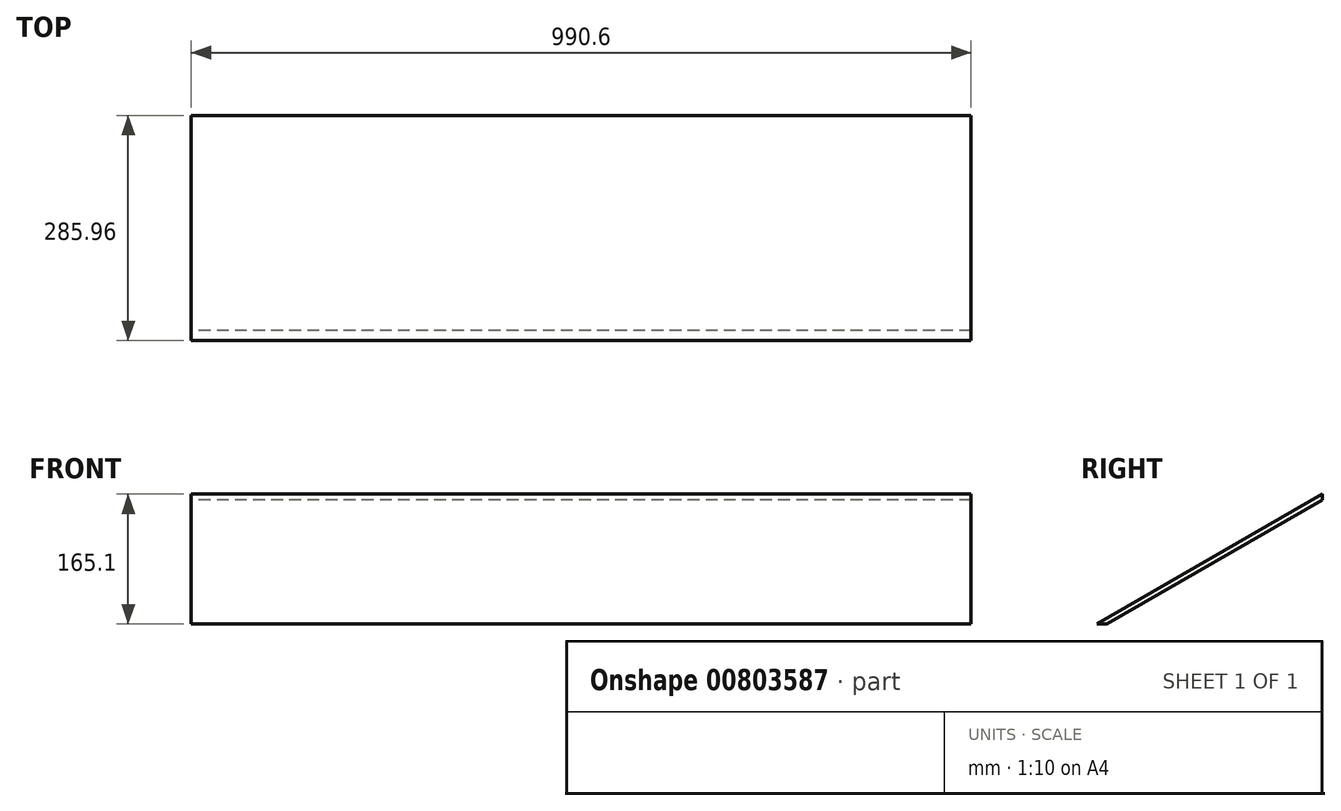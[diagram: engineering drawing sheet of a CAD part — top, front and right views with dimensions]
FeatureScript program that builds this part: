
annotation { "Feature Type Name" : "Feature", "Feature Type Description" : "" }
export const myFeature = defineFeature(function(context is Context, id is Id, definition is map)
    precondition{}
    {
        {
            var Q0;
            Q0=qCreatedBy(makeId("Right.planeOp"),FACE);
            var sketch = newSketch(context, id + "F0", { "sketchPlane" : qUnion([Q0])});
            skLineSegment(sketch, "E0", {"start": v(-285.96, 0) * mm, "end": v(0, 165.1) * mm});
            skLineSegment(sketch, "E1", {"start": v(-273.26, 0) * mm, "end": v(0, 157.77) * mm});
            skLineSegment(sketch, "E2", {"start": v(-285.96, 0) * mm, "end": v(-273.26, 0) * mm});
            skLineSegment(sketch, "E3", {"start": v(0, 157.77) * mm, "end": v(0, 165.1) * mm});
            skSolve(sketch);
        }
        {
            var Q0;
            Q0=makeQuery(id+"F0.imprint","IMPRINT",FACE,{"disambiguationData":[TD([[makeQuery(id+"F0.imprint","IMPRINT",EDGE,{"derivedFrom":sQuery(id+"F0.wireOp",EDGE,"E0")}),-1.0]])]});
            extrude(context, id + "F1", {"entities" : qUnion([Q0]), "endBound" : BoundingType.SYMMETRIC, "depth" : 990.6 * mm, "offsetDistance" : 25.4 * mm});
        }
    });
